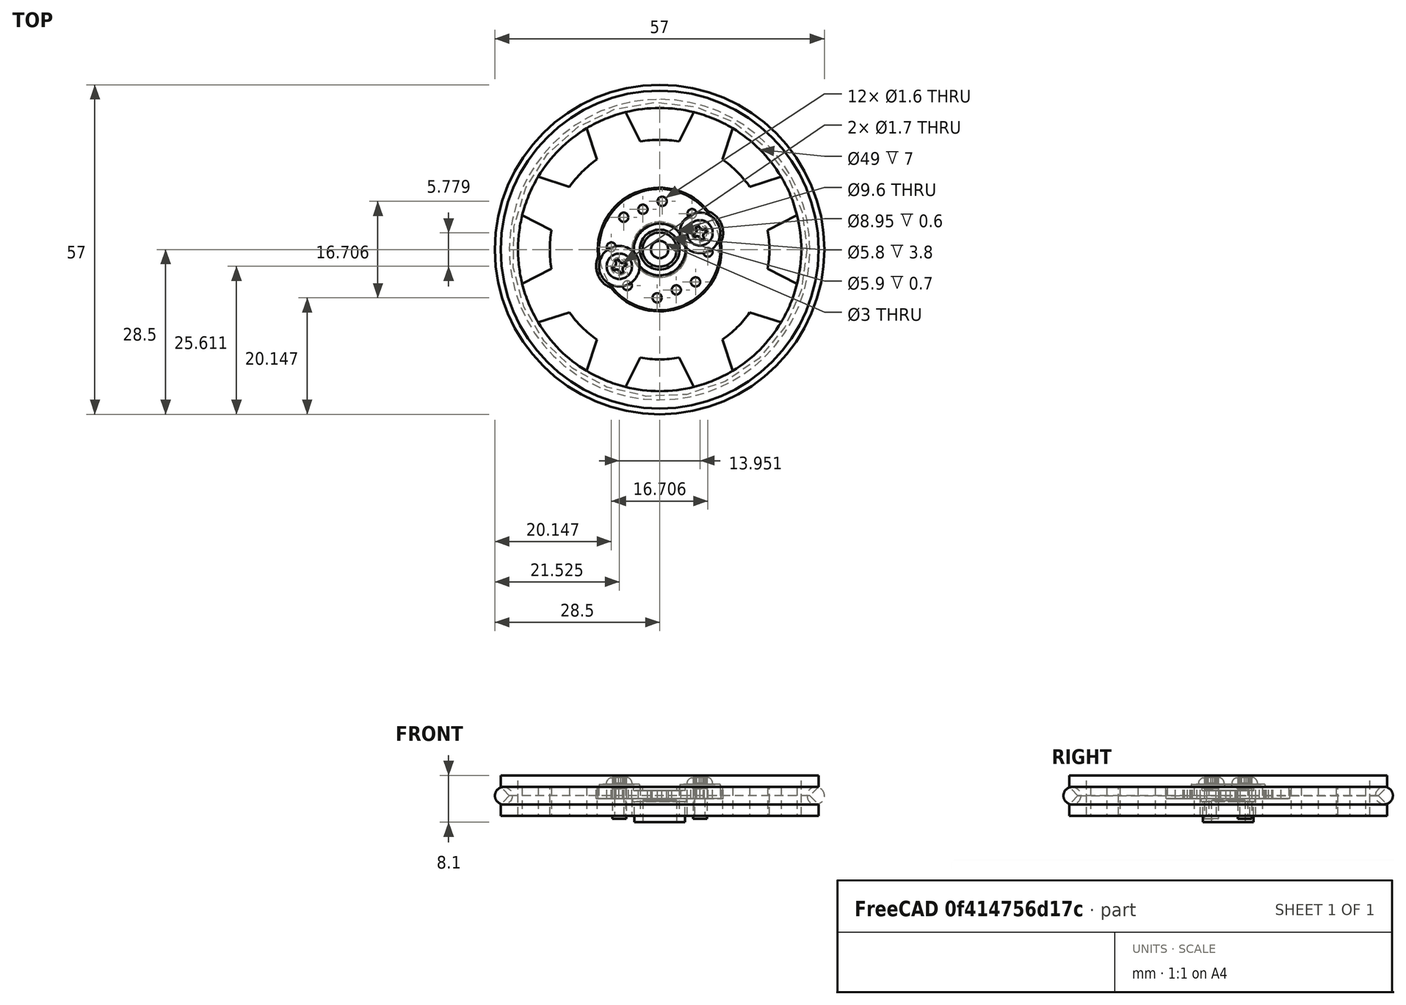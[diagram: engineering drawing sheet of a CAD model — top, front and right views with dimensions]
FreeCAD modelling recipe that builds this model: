
FCSTD DOCUMENT  (FreeCAD 0.14R3702 (Git))
Label: Renacuajo-wheel-gear-assembly
License: CC-BY 3.0
LicenseURL: http://creativecommons.org/licenses/by/3.0/
objects: Part::Feature×4, Part::Torus×1, Part::Compound×1
note: 6 computed .brp shape members not serialized (recipe doc carries the construction recipe); baked Part::Feature solids carry a one-line shape summary decoded from their .brp

FEATURE [Part::Feature] PolarPattern  label="Renacuajo-wheel-gear-final"
  Placement = pos=(0,0,0) rot=(1,0,0;1.5708rad)
  shape: bbox 55 x 55 x 7 mm, 41 faces (baked)
FEATURE [Part::Torus] Torus  label="o-ring"
  Angle1 = -180
  Angle2 = 180
  Angle3 = 360
  Radius1 = 27
  Radius2 = 1.5
FEATURE [Part::Feature] Chamfer  label="screw2"
  Placement = pos=(-6.97529,-2.88926,1.5) rot=(0,0,1;0.392699rad)
  shape: bbox 7 x 7 x 7.14 mm, 33 faces (baked)
FEATURE [Part::Feature] Chamfer001  label="screw1"
  Placement = pos=(6.97529,2.88926,1.5) rot=(0,0,1;0.392699rad)
  shape: bbox 7 x 7 x 7.14 mm, 33 faces (baked)
FEATURE [Part::Feature] Pocket  label="small-rounded-horn"
  Placement = pos=(0,0,-0.5) rot=(0,0,1;0.392699rad)
  shape: bbox 21 x 21 x 6.2 mm, 28 faces (baked)
FEATURE [Part::Compound] Compound  label="Renacuajo-wheel-gear-assembly-final"
  Links = -> [PolarPattern,Chamfer001,Torus,Chamfer,Pocket]
